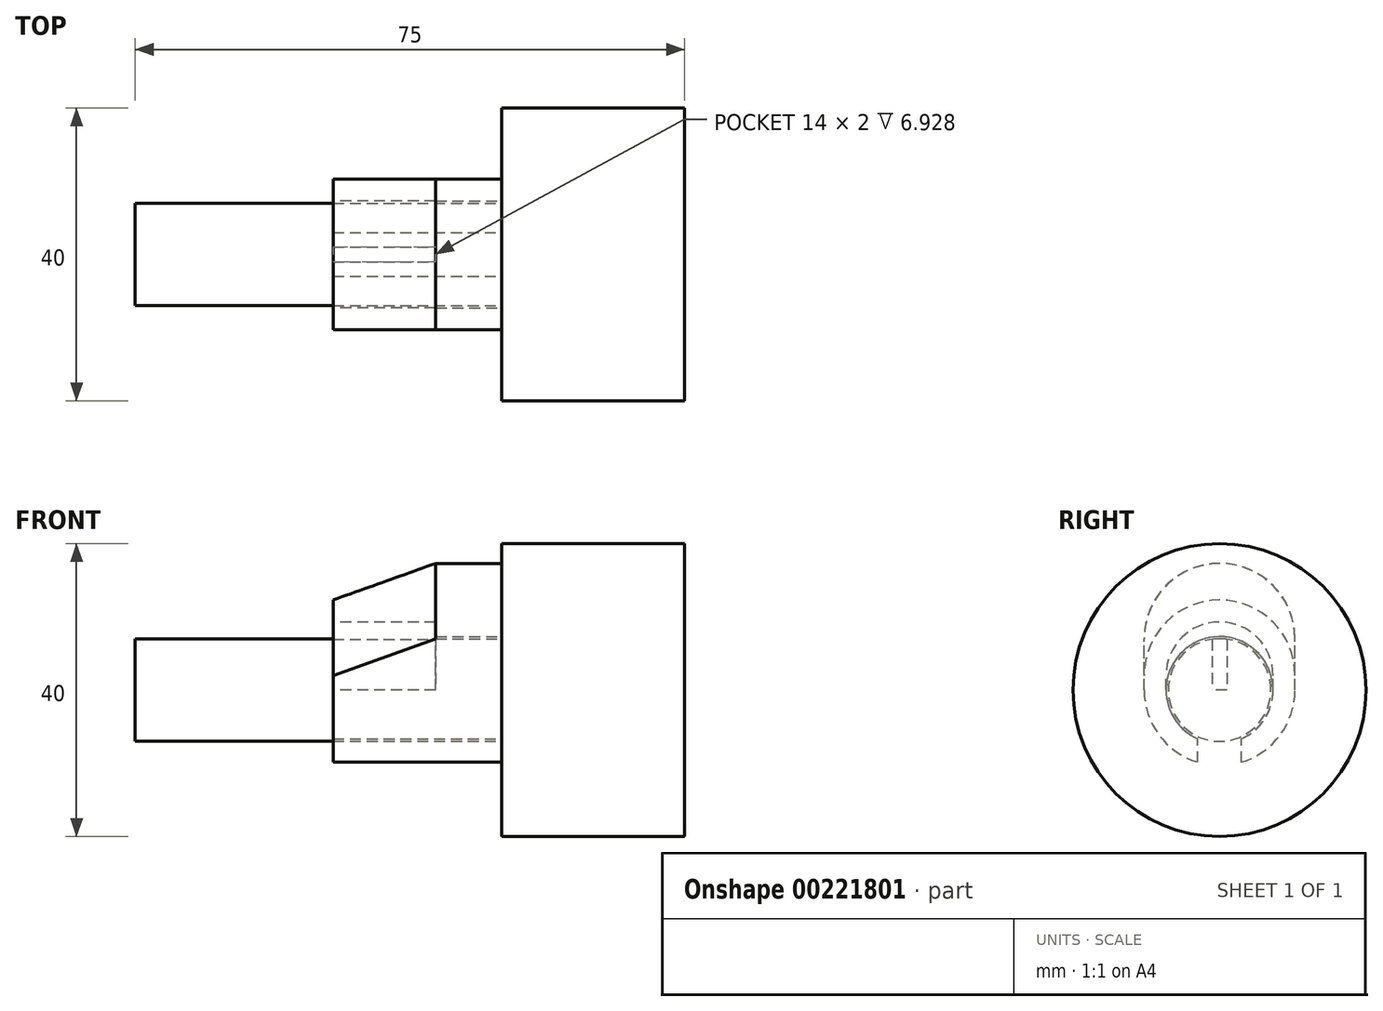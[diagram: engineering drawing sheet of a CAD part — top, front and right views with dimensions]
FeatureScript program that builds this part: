
annotation { "Feature Type Name" : "Feature", "Feature Type Description" : "" }
export const myFeature = defineFeature(function(context is Context, id is Id, definition is map)
    precondition{}
    {
        {
            var Q0;
            Q0=qCreatedBy(makeId("Right.planeOp"),FACE);
            var sketch = newSketch(context, id + "F0", { "sketchPlane" : qUnion([Q0])});
            skCircle(sketch, "E0", {"center": v(0, 0) * mm, "radius": 7 * mm});
            skCircle(sketch, "E1", {"center": v(0, 0) * mm, "radius": 20 * mm});
            skSolve(sketch);
        }
        {
            var Q0;
            Q0=makeQuery(id+"F0.imprint","IMPRINT",FACE,{"disambiguationData":[TD([[makeQuery(id+"F0.imprint","IMPRINT",EDGE,{"derivedFrom":sQuery(id+"F0.wireOp",EDGE,"E0")}),1.0]])]});
            extrude(context, id + "F1", {"entities" : qUnion([Q0]), "oppositeDirection" : true, "depth" : 50 * mm});
        }
        {
            var Q0;
            Q0=makeQuery(id+"F0.imprint","IMPRINT",FACE,{"disambiguationData":[TD([[makeQuery(id+"F0.imprint","IMPRINT",EDGE,{"derivedFrom":sQuery(id+"F0.wireOp",EDGE,"E0")}),-1.0]])]});
            var Q1;
            Q1=makeQuery(id+"F0.imprint","IMPRINT",FACE,{"disambiguationData":[TD([[makeQuery(id+"F0.imprint","IMPRINT",EDGE,{"derivedFrom":sQuery(id+"F0.wireOp",EDGE,"E0")}),1.0]])]});
            extrude(context, id + "F2", {"entities" : qUnion([Q0, Q1]), "operationType" : NewBodyOperationType.ADD, "depth" : 25 * mm});
        }
        {
            var Q0;
            Q0=qCreatedBy(makeId("Right.planeOp"),FACE);
            var sketch = newSketch(context, id + "F3", { "sketchPlane" : qUnion([Q0])});
            skCircle(sketch, "E2.0", {"center": v(0, 0) * mm, "radius": 7 * mm, "construction": true});
            skCircle(sketch, "E3.0", {"center": v(0, 0) * mm, "radius": 7.3 * mm});
            skCircle(sketch, "E4.0", {"center": v(0, 0) * mm, "radius": 10.3 * mm});
            skLineSegment(sketch, "E5", {"start": v(0, -10.3) * mm, "end": v(-3, -10.3) * mm});
            skLineSegment(sketch, "E6", {"start": v(-3, -10.3) * mm, "end": v(-3, 0) * mm});
            skLineSegment(sketch, "E7", {"start": v(-3, 0) * mm, "end": v(0, 0) * mm});
            skLineSegment(sketch, "E8.MirrorCS", {"start": v(0, -10.3) * mm, "end": v(3, -10.3) * mm});
            skLineSegment(sketch, "E9.MirrorCS", {"start": v(3, 0) * mm, "end": v(0, 0) * mm});
            skLineSegment(sketch, "E10.MirrorCS", {"start": v(3, -10.3) * mm, "end": v(3, 0) * mm});
            skLineSegment(sketch, "E11", {"start": v(-10.3, 0) * mm, "end": v(-10.3, 7) * mm});
            skLineSegment(sketch, "E12", {"start": v(10.3, 0) * mm, "end": v(10.3, 7) * mm});
            skArc(sketch, "E13", {"start": v(10.3, 7) * mm, "mid": v(0, 17.3) * mm, "end": v(-10.3, 7) * mm});
            skPoint(sketch, "E14", {"position": v(0, 7.3) * mm});
            skPoint(sketch, "E15", {"position": v(0, 17.3) * mm});
            skSolve(sketch);
        }
        {
            var Q0;
            {var subQ2=sQuery(id+"F3.wireOp",EDGE,"E6");var subQ6=sQuery(id+"F3.wireOp",EDGE,"E3.0");var subQ9=makeQuery(id+"F3.imprint","INTERSECT",VERTEX,{"derivedFrom":[subQ6,subQ2]});Q0=makeQuery(id+"F3.imprint","IMPRINT",FACE,{"disambiguationData":[TD([[makeQuery(id+"F3.imprint","IMPRINT",EDGE,{"disambiguationData":[TD([[subQ9,1.0]])],"derivedFrom":subQ6}),-1.0]])]});}
            var Q1;
            {var subQ0=sQuery(id+"F3.wireOp",EDGE,"E11");Q1=makeQuery(id+"F3.imprint","IMPRINT",FACE,{"disambiguationData":[TD([[makeQuery(id+"F3.imprint","IMPRINT",EDGE,{"derivedFrom":subQ0}),-1.0]])]});}
            extrude(context, id + "F4", {"entities" : qUnion([Q0, Q1]), "oppositeDirection" : true, "depth" : 9 * mm});
        }
        {
            var Q0;
            Q0=qCreatedBy(makeId("Right.planeOp"),FACE);
            cPlane(context, id + "F5", {"entities" : qUnion([Q0]), "cplaneType" : CPlaneType.OFFSET, "offset" : 23 * mm, "oppositeDirection" : true, "width" : 150 * mm, "height" : 150 * mm});
        }
        {
            var Q0;
            Q0=qCreatedBy(id+"F5.planeOp",FACE);
            var sketch = newSketch(context, id + "F6", { "sketchPlane" : qUnion([Q0])});
            skCircle(sketch, "E16.0", {"center": v(0, 0) * mm, "radius": 7.3 * mm});
            skCircle(sketch, "E16.1", {"center": v(0, 0) * mm, "radius": 10.3 * mm, "construction": true});
            skLineSegment(sketch, "E17.0", {"start": v(0, -10.3) * mm, "end": v(3, -10.3) * mm});
            skLineSegment(sketch, "E17.1", {"start": v(3, -10.3) * mm, "end": v(3, 0) * mm});
            skLineSegment(sketch, "E17.2", {"start": v(3, 0) * mm, "end": v(0, 0) * mm});
            skLineSegment(sketch, "E17.3", {"start": v(-3, 0) * mm, "end": v(0, 0) * mm});
            skLineSegment(sketch, "E17.4", {"start": v(-3, -10.3) * mm, "end": v(-3, 0) * mm});
            skLineSegment(sketch, "E17.5", {"start": v(0, -10.3) * mm, "end": v(-3, -10.3) * mm});
            skLineSegment(sketch, "E18", {"start": v(-10.3, 0) * mm, "end": v(-10.3, 2) * mm});
            skLineSegment(sketch, "E19", {"start": v(10.3, 0) * mm, "end": v(10.3, 2) * mm});
            skArc(sketch, "E20", {"start": v(10.3, 2) * mm, "mid": v(0, 12.3) * mm, "end": v(-10.3, 2) * mm});
            skPoint(sketch, "E21", {"position": v(0, 12.3) * mm});
            skArc(sketch, "E22", {"start": v(10.3, 0) * mm, "mid": v(0, -10.3) * mm, "end": v(-10.3, 0) * mm});
            skSolve(sketch);
        }
        {
            var Q1;
            {var subQ0=sQuery(id+"F6.wireOp",EDGE,"E18");Q1=makeQuery(id+"F6.imprint","IMPRINT",FACE,{"disambiguationData":[TD([[makeQuery(id+"F6.imprint","IMPRINT",EDGE,{"derivedFrom":subQ0}),-1.0]])]});}
            var Q2;
            Q2=makeQuery(id+"F4.opExtrude","CAP_FACE",FACE,{"disambiguationData":[OSD([sQuery(id+"F3.wireOp",EDGE,"E3.0"),sQuery(id+"F3.wireOp",EDGE,"E4.0"),sQuery(id+"F3.wireOp",EDGE,"E6"),sQuery(id+"F3.wireOp",EDGE,"E10.MirrorCS"),sQuery(id+"F3.wireOp",EDGE,"E11"),sQuery(id+"F3.wireOp",EDGE,"E12"),sQuery(id+"F3.wireOp",EDGE,"E13")])],"isStart":false});
            loft(context, id + "F7", {"operationType" : NewBodyOperationType.ADD, "sheetProfilesArray" : [{ "sheetProfileEntities" : qUnion([Q1]) }, { "sheetProfileEntities" : qUnion([Q2]) }]});
        }
        {
            var Q0;
            {var subQ0=sQuery(id+"F6.wireOp",EDGE,"E18");Q0=makeQuery(id+"F7.opLoft","CAP_FACE",FACE,{"disambiguationData":[OSD([makeQuery(id+"F6.imprint","IMPRINT",FACE,{"disambiguationData":[TD([[makeQuery(id+"F6.imprint","IMPRINT",EDGE,{"derivedFrom":subQ0}),-1.0]])]})])],"isStart":true});}
            var sketch = newSketch(context, id + "F8", { "sketchPlane" : qUnion([Q0])});
            skFitSpline(sketch, "E23.0", {"points": [v(-10.3, 2) * mm, v(-10.3, 2.42) * mm, v(-10.25, 3.36) * mm, v(-9.91, 4.99) * mm, v(-9.22, 6.73) * mm, v(-8.11, 8.46) * mm, v(-6.57, 10.04) * mm, v(-4.64, 11.3) * mm, v(-2.4, 12.11) * mm, v(0, 12.4) * mm, v(2.4, 12.11) * mm, v(4.64, 11.3) * mm, v(6.57, 10.04) * mm, v(8.11, 8.46) * mm, v(9.22, 6.73) * mm, v(9.91, 4.99) * mm, v(10.25, 3.36) * mm, v(10.3, 2.42) * mm, v(10.3, 2) * mm]});
            skArc(sketch, "E23.1", {"start": v(3, -6.66) * mm, "mid": v(0, 7.3) * mm, "end": v(-3, -6.66) * mm});
            skPoint(sketch, "E24", {"position": v(0, 12.3) * mm});
            skLineSegment(sketch, "E25", {"start": v(7.3, 0) * mm, "end": v(7.3, 2) * mm});
            skLineSegment(sketch, "E26", {"start": v(-7.3, 0) * mm, "end": v(-7.3, 2) * mm});
            skArc(sketch, "E27", {"start": v(-7.3, 2) * mm, "mid": v(0, 9.3) * mm, "end": v(7.3, 2) * mm});
            skPoint(sketch, "E28", {"position": v(0, 9.3) * mm});
            skSolve(sketch);
        }
        {
            var Q0;
            {var subQ0=sQuery(id+"F8.wireOp",EDGE,"E25");Q0=makeQuery(id+"F8.imprint","IMPRINT",FACE,{"disambiguationData":[TD([[makeQuery(id+"F8.imprint","IMPRINT",EDGE,{"derivedFrom":subQ0}),1.0]])]});}
            var Q1;
            {var subQ0=sQuery(id+"F3.wireOp",EDGE,"E13");var subQ1=sQuery(id+"F3.wireOp",EDGE,"E12");Q1=makeQuery(id+"F7.boolean.opBoolean","MERGE",VERTEX,{"derivedFrom":[makeQuery(id+"F4.opExtrude","CAP_VERTEX",VERTEX,{"disambiguationData":[OSD([subQ1,subQ0])],"isStart":false}),makeQuery(id+"F7.opLoft","MID_CAP_VERTEX",VERTEX,{"disambiguationData":[OSD([subQ1,subQ0])],"capPos":1.0})]});}
            extrude(context, id + "F9", {"entities" : qUnion([Q0]), "operationType" : NewBodyOperationType.REMOVE, "endBound" : BoundingType.UP_TO_VERTEX, "oppositeDirection" : true, "endBoundEntityVertex" : qUnion([Q1]), "depth" : 25 * mm});
        }
        {
            var Q0;
            {var subQ0=sQuery(id+"F6.wireOp",EDGE,"E17.1");var subQ1=sQuery(id+"F6.wireOp",EDGE,"E16.0");var subQ2=makeQuery(id+"F6.imprint","INTERSECT",VERTEX,{"derivedFrom":[subQ1,subQ0]});Q0=makeQuery(id+"F7.opLoft","CAP_FACE",FACE,{"disambiguationData":[OSD([makeQuery(id+"F6.imprint","IMPRINT",FACE,{"disambiguationData":[TD([[makeQuery(id+"F6.imprint","IMPRINT",EDGE,{"disambiguationData":[TD([[subQ2,-1.0]])],"derivedFrom":subQ1}),-1.0]])]})])],"isStart":true});}
            var sketch = newSketch(context, id + "F10", { "sketchPlane" : qUnion([Q0])});
            skArc(sketch, "E29.0", {"start": v(-10.3, 7) * mm, "mid": v(0, 17.3) * mm, "end": v(10.3, 7) * mm});
            skLineSegment(sketch, "E30", {"start": v(0, 17.3) * mm, "end": v(1, 17.3) * mm});
            skLineSegment(sketch, "E31", {"start": v(1, 17.3) * mm, "end": v(1, 0) * mm});
            skLineSegment(sketch, "E32", {"start": v(1, 0) * mm, "end": v(0, 0) * mm});
            skLineSegment(sketch, "E33.MirrorCS", {"start": v(-1, 0) * mm, "end": v(0, 0) * mm});
            skLineSegment(sketch, "E34.MirrorCS", {"start": v(-1, 17.3) * mm, "end": v(-1, 0) * mm});
            skLineSegment(sketch, "E35.MirrorCS", {"start": v(0, 17.3) * mm, "end": v(-1, 17.3) * mm});
            skSolve(sketch);
        }
        {
            var Q0;
            {var subQ1=sQuery(id+"F10.wireOp",EDGE,"E29.0");var subQ6=sQuery(id+"F10.wireOp",EDGE,"E34.MirrorCS");var subQ7=makeQuery(id+"F10.imprint","INTERSECT",VERTEX,{"derivedFrom":[subQ1,subQ6]});Q0=makeQuery(id+"F10.imprint","IMPRINT",FACE,{"disambiguationData":[TD([[makeQuery(id+"F10.imprint","IMPRINT",EDGE,{"disambiguationData":[TD([[subQ7,-1.0]])],"derivedFrom":subQ1}),-1.0]])]});}
            var Q1;
            {var subQ0=sQuery(id+"F10.wireOp",EDGE,"E31");var subQ3=makeQuery(id+"F7.opLoft","MID_CAP_EDGE",EDGE,{"disambiguationData":[OSD([sQuery(id+"F6.wireOp",EDGE,"E16.0"),sQuery(id+"F6.wireOp",EDGE,"E17.1"),sQuery(id+"F6.wireOp",EDGE,"E17.4")])],"capPos":0.0});var subQ4=makeQuery(id+"F10.imprint","INTERSECT",VERTEX,{"derivedFrom":[subQ3,subQ0]});Q1=makeQuery(id+"F10.imprint","IMPRINT",FACE,{"disambiguationData":[TD([[makeQuery(id+"F10.imprint","IMPRINT",EDGE,{"disambiguationData":[TD([[subQ4,1.0]])],"derivedFrom":subQ0}),-1.0]])]});}
            var Q2;
            {var subQ4=sQuery(id+"F10.wireOp",EDGE,"E32");Q2=makeQuery(id+"F10.imprint","IMPRINT",FACE,{"disambiguationData":[TD([[makeQuery(id+"F10.imprint","IMPRINT",EDGE,{"derivedFrom":subQ4}),-1.0]])]});}
            var Q3;
            {var subQ0=sQuery(id+"F10.wireOp",EDGE,"E31");var subQ3=makeQuery(id+"F9.boolean.opBoolean","COPY",EDGE,{"derivedFrom":makeQuery(id+"F9.opExtrude","CAP_EDGE",EDGE,{"disambiguationData":[OSD([sQuery(id+"F8.wireOp",EDGE,"E27")])],"isStart":true})});var subQ4=makeQuery(id+"F10.imprint","INTERSECT",VERTEX,{"derivedFrom":[subQ3,subQ0]});Q3=makeQuery(id+"F10.imprint","IMPRINT",FACE,{"disambiguationData":[TD([[makeQuery(id+"F10.imprint","IMPRINT",EDGE,{"disambiguationData":[TD([[subQ4,1.0]])],"derivedFrom":subQ3}),1.0]])]});}
            var Q4;
            Q4=makeQuery(id+"F4.opExtrude","CAP_FACE",FACE,{"disambiguationData":[OSD([sQuery(id+"F3.wireOp",EDGE,"E3.0"),sQuery(id+"F3.wireOp",EDGE,"E4.0"),sQuery(id+"F3.wireOp",EDGE,"E6"),sQuery(id+"F3.wireOp",EDGE,"E10.MirrorCS"),sQuery(id+"F3.wireOp",EDGE,"E11"),sQuery(id+"F3.wireOp",EDGE,"E12"),sQuery(id+"F3.wireOp",EDGE,"E13")])],"isStart":false});
            var Q5;
            {var subQ0=sQuery(id+"F3.wireOp",EDGE,"E13");var subQ1=sQuery(id+"F3.wireOp",EDGE,"E12");Q5=makeQuery(id+"F7.boolean.opBoolean","MERGE",VERTEX,{"derivedFrom":[makeQuery(id+"F4.opExtrude","CAP_VERTEX",VERTEX,{"disambiguationData":[OSD([subQ1,subQ0])],"isStart":false}),makeQuery(id+"F7.opLoft","MID_CAP_VERTEX",VERTEX,{"disambiguationData":[OSD([subQ1,subQ0])],"capPos":1.0})]});}
            extrude(context, id + "F11", {"entities" : qUnion([Q0, Q1, Q2, Q3]), "operationType" : NewBodyOperationType.REMOVE, "endBound" : BoundingType.UP_TO_VERTEX, "oppositeDirection" : true, "endBoundEntityFace" : qUnion([Q4]), "endBoundEntityVertex" : qUnion([Q5]), "depth" : 16 * mm});
        }
    });
